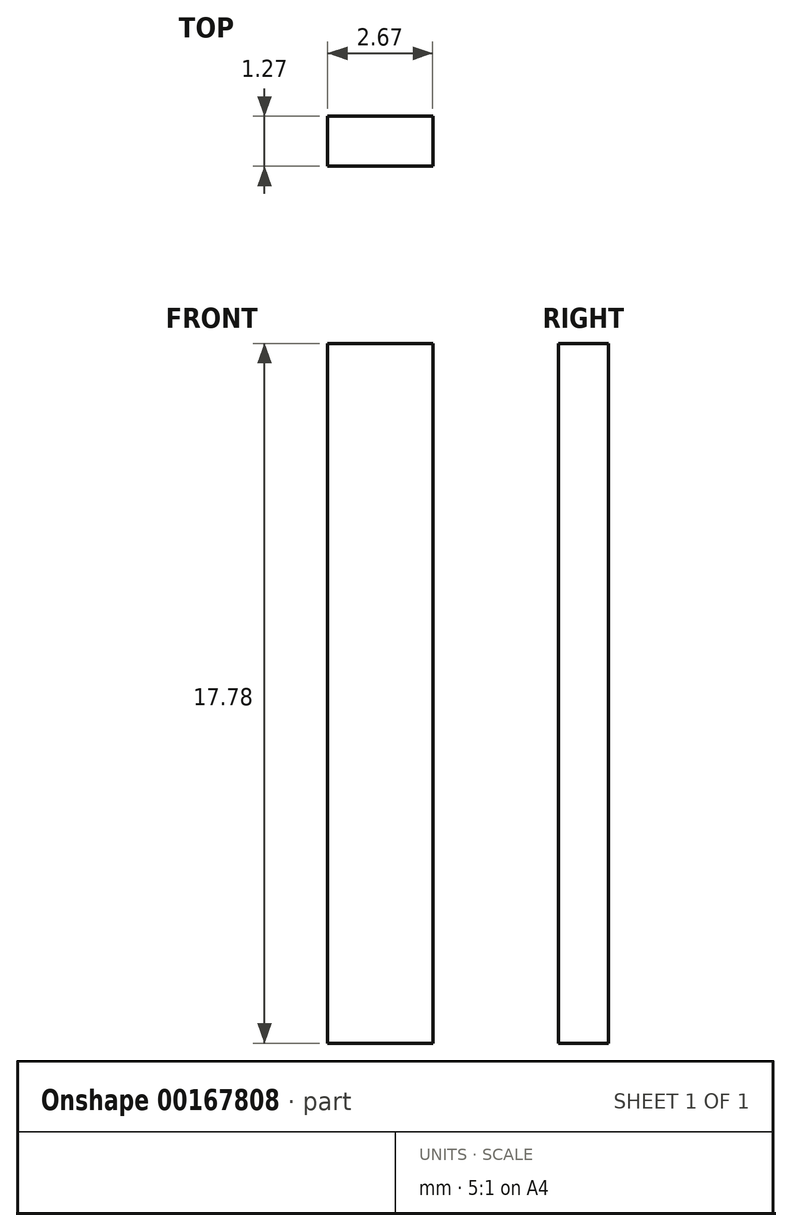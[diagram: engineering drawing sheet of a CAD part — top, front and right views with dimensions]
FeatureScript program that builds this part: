
annotation { "Feature Type Name" : "Feature", "Feature Type Description" : "" }
export const myFeature = defineFeature(function(context is Context, id is Id, definition is map)
    precondition{}
    {
        {
            var Q0;
            Q0=qCreatedBy(makeId("Front.planeOp"),FACE);
            var sketch = newSketch(context, id + "F0", { "sketchPlane" : qUnion([Q0])});
            skLineSegment(sketch, "E0.bottom", {"start": v(-56.21, 48.03) * mm, "end": v(-53.54, 48.03) * mm});
            skLineSegment(sketch, "E0.top", {"start": v(-56.21, 30.25) * mm, "end": v(-53.54, 30.25) * mm});
            skLineSegment(sketch, "E0.left", {"start": v(-56.21, 48.03) * mm, "end": v(-56.21, 30.25) * mm});
            skLineSegment(sketch, "E0.right", {"start": v(-53.54, 48.03) * mm, "end": v(-53.54, 30.25) * mm});
            skSolve(sketch);
        }
        {
            var Q0;
            Q0=makeQuery(id+"F0.imprint","IMPRINT",FACE,{"disambiguationData":[TD([[makeQuery(id+"F0.imprint","IMPRINT",EDGE,{"derivedFrom":sQuery(id+"F0.wireOp",EDGE,"E0.bottom")}),-1.0]])]});
            extrude(context, id + "F1", {"entities" : qUnion([Q0]), "depth" : 1.27 * mm});
        }
    });
